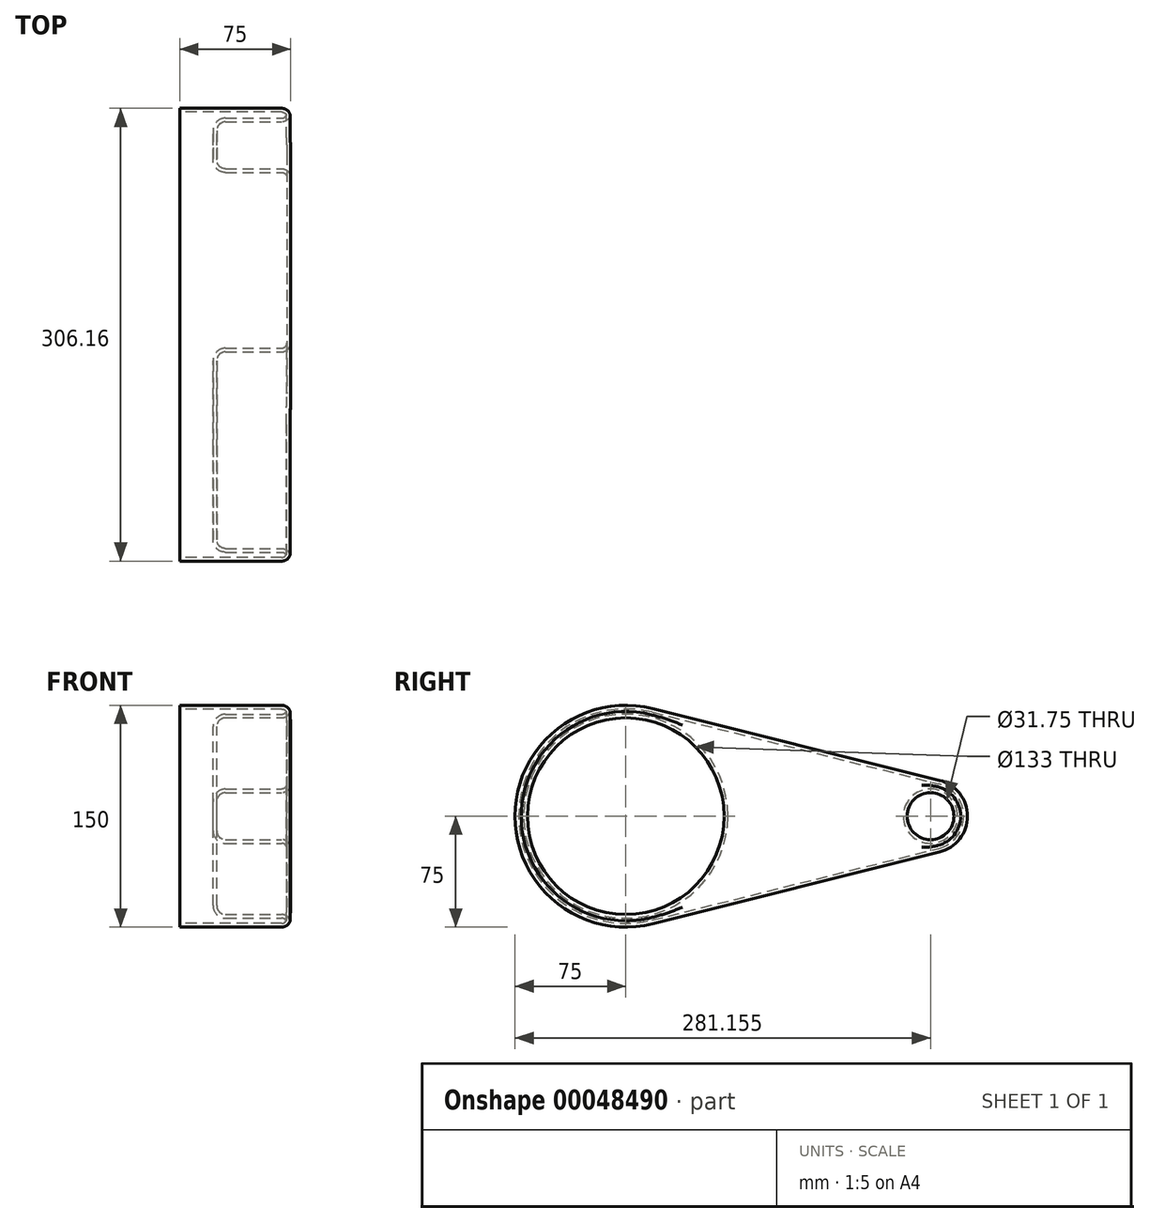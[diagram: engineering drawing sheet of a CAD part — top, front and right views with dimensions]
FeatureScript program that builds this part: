
annotation { "Feature Type Name" : "Feature", "Feature Type Description" : "" }
export const myFeature = defineFeature(function(context is Context, id is Id, definition is map)
    precondition{}
    {
        {
            var Q0;
            Q0=qCreatedBy(makeId("Right.planeOp"),FACE);
            var sketch = newSketch(context, id + "F0", { "sketchPlane" : qUnion([Q0])});
            skCircle(sketch, "E0", {"center": v(0, 0) * mm, "radius": 75 * mm});
            skCircle(sketch, "E1", {"center": v(206.16, 0) * mm, "radius": 25 * mm});
            skLineSegment(sketch, "E2", {"start": v(18.2, 72.76) * mm, "end": v(212.22, 24.25) * mm});
            skLineSegment(sketch, "E3", {"start": v(18.2, -72.76) * mm, "end": v(212.22, -24.25) * mm});
            skSolve(sketch);
        }
        {
            var Q0;
            {var subQ0=sQuery(id+"F0.wireOp",EDGE,"E0");var subQ2=makeQuery(id+"F0.imprint","INTERSECT",VERTEX,{"derivedFrom":[subQ0,sQuery(id+"F0.wireOp",EDGE,"E2")]});Q0=makeQuery(id+"F0.imprint","IMPRINT",FACE,{"disambiguationData":[TD([[makeQuery(id+"F0.imprint","IMPRINT",EDGE,{"disambiguationData":[TD([[subQ2,-1.0]])],"derivedFrom":subQ0}),1.0]])]});}
            var Q1;
            {var subQ1=sQuery(id+"F0.wireOp",EDGE,"E2");Q1=makeQuery(id+"F0.imprint","IMPRINT",FACE,{"disambiguationData":[TD([[makeQuery(id+"F0.imprint","IMPRINT",EDGE,{"derivedFrom":subQ1}),-1.0]])]});}
            var Q2;
            {var subQ0=sQuery(id+"F0.wireOp",EDGE,"E1");var subQ2=makeQuery(id+"F0.imprint","INTERSECT",VERTEX,{"derivedFrom":[subQ0,sQuery(id+"F0.wireOp",EDGE,"E2")]});Q2=makeQuery(id+"F0.imprint","IMPRINT",FACE,{"disambiguationData":[TD([[makeQuery(id+"F0.imprint","IMPRINT",EDGE,{"disambiguationData":[TD([[subQ2,-1.0]])],"derivedFrom":subQ0}),1.0]])]});}
            extrude(context, id + "F1", {"entities" : qUnion([Q0, Q1, Q2]), "depth" : 75 * mm});
        }
        {
            var Q0;
            Q0=makeQuery(id+"F1.opExtrude","CAP_FACE",FACE,{"disambiguationData":[OSD([sQuery(id+"F0.wireOp",EDGE,"E0"),sQuery(id+"F0.wireOp",EDGE,"E1"),sQuery(id+"F0.wireOp",EDGE,"E2"),sQuery(id+"F0.wireOp",EDGE,"E3")])],"isStart":false});
            var sketch = newSketch(context, id + "F2", { "sketchPlane" : qUnion([Q0])});
            skCircle(sketch, "E4", {"center": v(0, 0) * mm, "radius": 66.5 * mm});
            skCircle(sketch, "E5", {"center": v(206.16, 0) * mm, "radius": 15.88 * mm});
            skSolve(sketch);
        }
        {
            var Q0;
            Q0=makeQuery(id+"F2.imprint","IMPRINT",FACE,{"disambiguationData":[TD([[makeQuery(id+"F2.imprint","IMPRINT",EDGE,{"derivedFrom":sQuery(id+"F2.wireOp",EDGE,"E4")}),1.0]])]});
            var Q1;
            Q1=makeQuery(id+"F2.imprint","IMPRINT",FACE,{"disambiguationData":[TD([[makeQuery(id+"F2.imprint","IMPRINT",EDGE,{"derivedFrom":sQuery(id+"F2.wireOp",EDGE,"E5")}),1.0]])]});
            extrude(context, id + "F3", {"entities" : qUnion([Q0, Q1]), "operationType" : NewBodyOperationType.REMOVE, "oppositeDirection" : true, "depth" : 50 * mm});
        }
        {
            var Q0;
            Q0=makeQuery(id+"F3.boolean.opBoolean","COPY",FACE,{"derivedFrom":makeQuery(id+"F3.opExtrude","SWEPT_FACE",FACE,{"disambiguationData":[OSD([sQuery(id+"F2.wireOp",EDGE,"E4")])]})});
            var Q1;
            Q1=makeQuery(id+"F1.opExtrude","CAP_FACE",FACE,{"disambiguationData":[OSD([sQuery(id+"F0.wireOp",EDGE,"E0"),sQuery(id+"F0.wireOp",EDGE,"E1"),sQuery(id+"F0.wireOp",EDGE,"E2"),sQuery(id+"F0.wireOp",EDGE,"E3")])],"isStart":false});
            var Q2;
            Q2=makeQuery(id+"F3.boolean.opBoolean","COPY",FACE,{"derivedFrom":makeQuery(id+"F3.opExtrude","CAP_FACE",FACE,{"disambiguationData":[OSD([sQuery(id+"F2.wireOp",EDGE,"E5")])],"isStart":false})});
            fillet(context, id + "F4", {"entities" : qUnion([Q0, Q1, Q2]), "radius" : 6 * mm, "tangentPropagation" : true, "allowEdgeOverflow" : false});
        }
        {
            var Q0;
            Q0=makeQuery(id+"F1.opExtrude","CAP_FACE",FACE,{"disambiguationData":[OSD([sQuery(id+"F0.wireOp",EDGE,"E0"),sQuery(id+"F0.wireOp",EDGE,"E1"),sQuery(id+"F0.wireOp",EDGE,"E2"),sQuery(id+"F0.wireOp",EDGE,"E3")])],"isStart":true});
            shell(context, id + "F5", {"entities" : qUnion([Q0]), "thickness" : 2.5 * mm});
        }
    });
